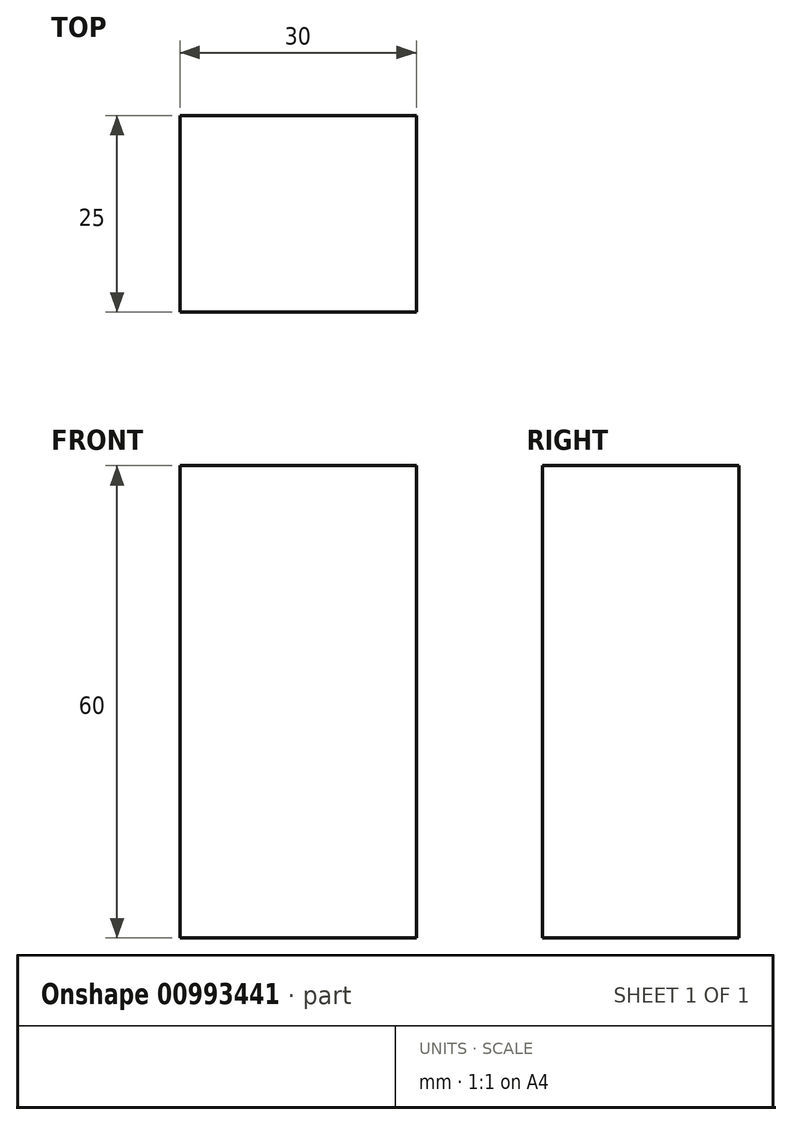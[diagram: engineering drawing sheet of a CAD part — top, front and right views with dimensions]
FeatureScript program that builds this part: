
annotation { "Feature Type Name" : "Feature", "Feature Type Description" : "" }
export const myFeature = defineFeature(function(context is Context, id is Id, definition is map)
    precondition{}
    {
        {
            var Q0;
            Q0=qCreatedBy(makeId("Front.planeOp"),FACE);
            var sketch = newSketch(context, id + "F0", { "sketchPlane" : qUnion([Q0])});
            skLineSegment(sketch, "E0.bottom", {"start": v(-15, 60) * mm, "end": v(15, 60) * mm});
            skLineSegment(sketch, "E0.top", {"start": v(-15, 0) * mm, "end": v(15, 0) * mm});
            skLineSegment(sketch, "E0.left", {"start": v(-15, 60) * mm, "end": v(-15, 0) * mm});
            skLineSegment(sketch, "E0.right", {"start": v(15, 60) * mm, "end": v(15, 0) * mm});
            skSolve(sketch);
        }
        {
            var Q0;
            Q0 = qSketchRegion(id + "F0", true);
            extrude(context, id + "F1", {"entities" : qUnion([Q0]), "depth" : 25 * mm, "offsetDistance" : 25 * mm});
        }
    });
